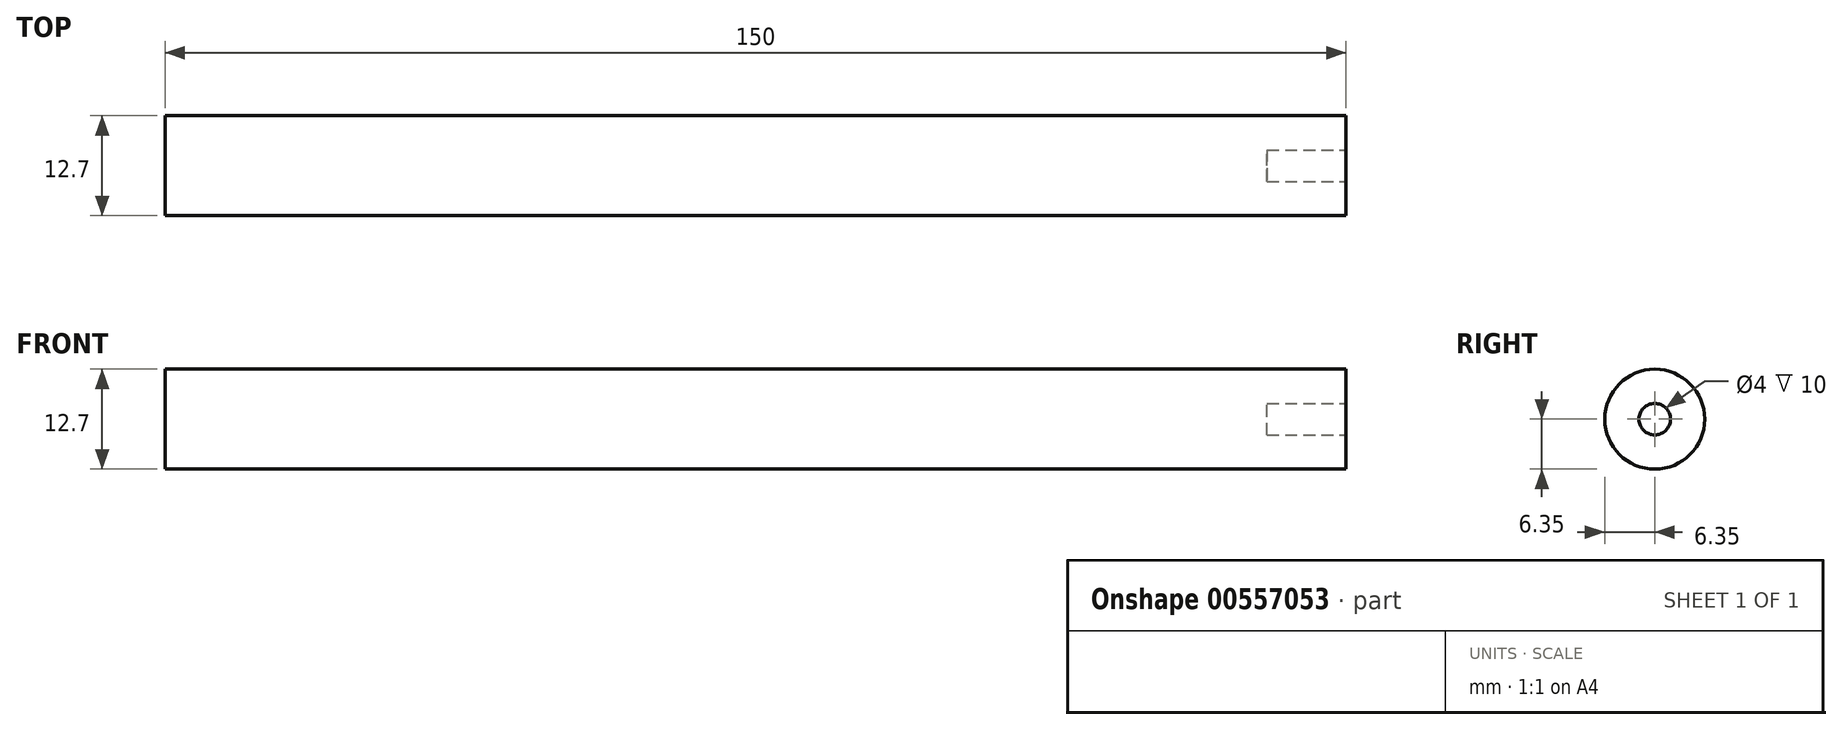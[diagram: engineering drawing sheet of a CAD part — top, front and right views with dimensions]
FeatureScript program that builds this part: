
annotation { "Feature Type Name" : "Feature", "Feature Type Description" : "" }
export const myFeature = defineFeature(function(context is Context, id is Id, definition is map)
    precondition{}
    {
        {
            var Q0;
            Q0=qCreatedBy(makeId("Right.planeOp"),FACE);
            var sketch = newSketch(context, id + "F0", { "sketchPlane" : qUnion([Q0])});
            skCircle(sketch, "E0", {"center": v(0, 0) * mm, "radius": 6.35 * mm});
            skSolve(sketch);
        }
        {
            var Q0;
            Q0=makeQuery(id+"F0.imprint","IMPRINT",FACE,{"disambiguationData":[TD([[makeQuery(id+"F0.imprint","IMPRINT",EDGE,{"derivedFrom":sQuery(id+"F0.wireOp",EDGE,"E0")}),1.0]])]});
            extrude(context, id + "F1", {"entities" : qUnion([Q0]), "depth" : 150 * mm, "offsetDistance" : 25 * mm});
        }
        {
            var Q0;
            Q0=makeQuery(id+"F1.opExtrude","CAP_FACE",FACE,{"disambiguationData":[OSD([sQuery(id+"F0.wireOp",EDGE,"E0")])],"isStart":false});
            var sketch = newSketch(context, id + "F2", { "sketchPlane" : qUnion([Q0])});
            skCircle(sketch, "E1", {"center": v(0, 0) * mm, "radius": 2 * mm});
            skSolve(sketch);
        }
        {
            var Q0;
            Q0=makeQuery(id+"F2.imprint","IMPRINT",FACE,{"disambiguationData":[TD([[makeQuery(id+"F2.imprint","IMPRINT",EDGE,{"derivedFrom":sQuery(id+"F2.wireOp",EDGE,"E1")}),1.0]])]});
            var Q1;
            Q1=sQuery(id+"F2.wireOp",EDGE,"E1");
            extrude(context, id + "F3", {"entities" : qUnion([Q0]), "operationType" : NewBodyOperationType.REMOVE, "surfaceEntities" : qUnion([Q1]), "oppositeDirection" : true, "depth" : 10 * mm, "offsetDistance" : 25 * mm});
        }
    });
